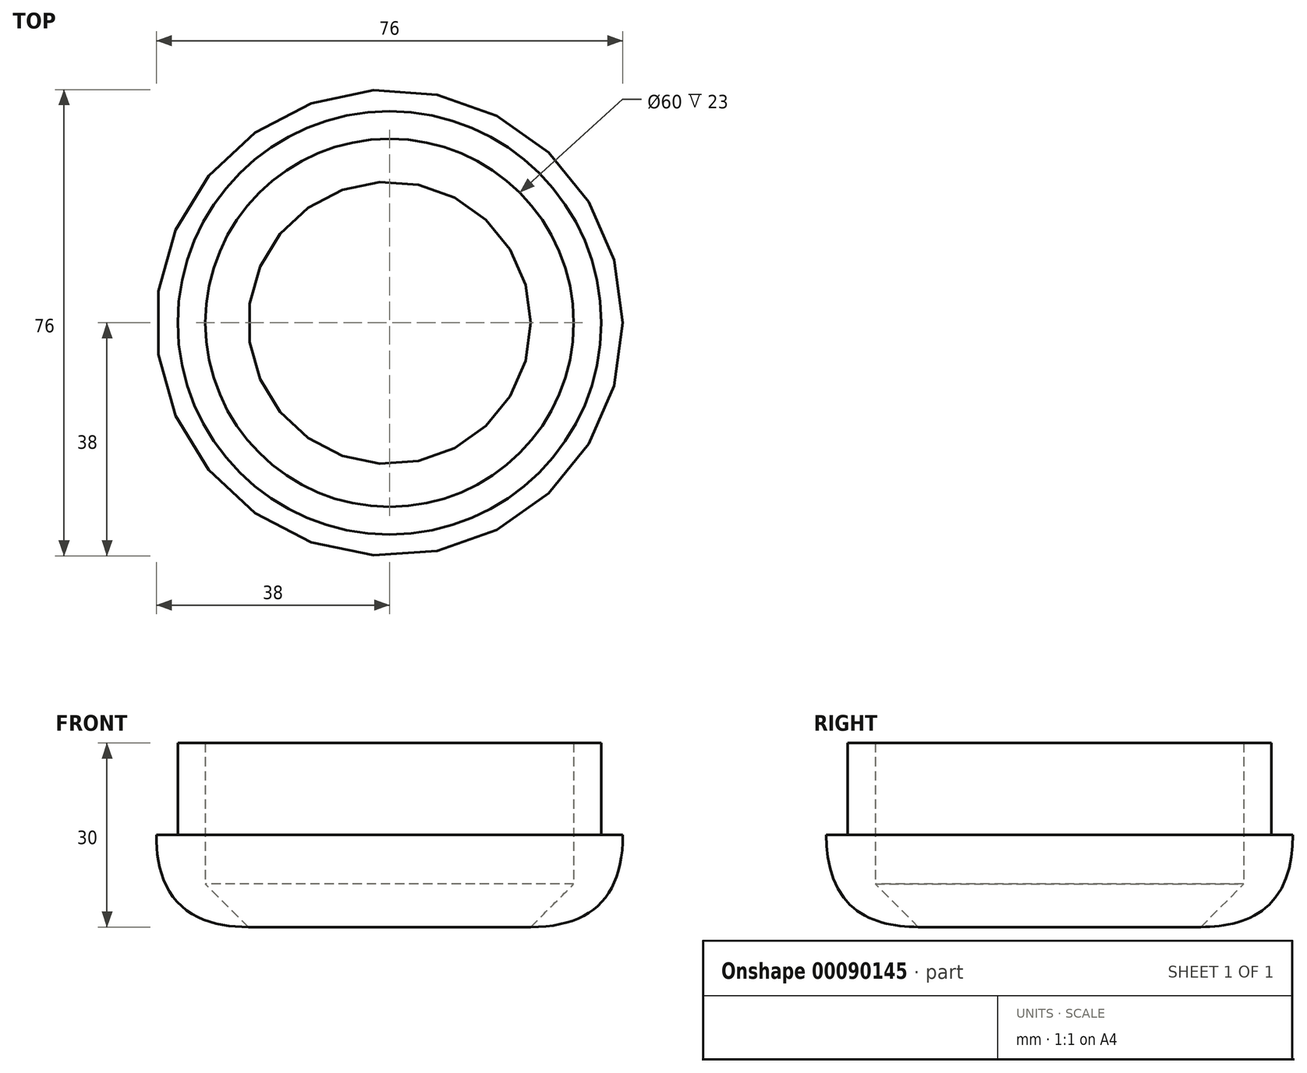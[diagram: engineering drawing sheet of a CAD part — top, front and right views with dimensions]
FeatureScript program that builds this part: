
annotation { "Feature Type Name" : "Feature", "Feature Type Description" : "" }
export const myFeature = defineFeature(function(context is Context, id is Id, definition is map)
    precondition{}
    {
        {
            var Q0;
            Q0=qCreatedBy(makeId("Top.planeOp"),FACE);
            var sketch = newSketch(context, id + "F0", { "sketchPlane" : qUnion([Q0])});
            skCircle(sketch, "E0", {"center": v(0, 0) * mm, "radius": 34.5 * mm});
            skCircle(sketch, "E1", {"center": v(0, 0) * mm, "radius": 30 * mm});
            skCircle(sketch, "E2", {"center": v(0, 0) * mm, "radius": 38 * mm});
            skCircle(sketch, "E3", {"center": v(0, 0) * mm, "radius": 23 * mm});
            skSolve(sketch);
        }
        {
            var Q0;
            Q0=qSketchRegion(id+"F0",true);
            extrude(context, id + "F1", {"entities" : qUnion([Q0]), "depth" : 15 * mm});
        }
        {
            var Q0;
            Q0=makeQuery(id+"F0.imprint","IMPRINT",FACE,{"disambiguationData":[TD([[makeQuery(id+"F0.imprint","IMPRINT",EDGE,{"derivedFrom":sQuery(id+"F0.wireOp",EDGE,"E0")}),1.0]])]});
            extrude(context, id + "F2", {"entities" : qUnion([Q0]), "operationType" : NewBodyOperationType.ADD, "depth" : 30 * mm});
        }
        {
            var Q0;
            Q0=qSketchRegion(id+"F0",true);
            var Q1;
            Q1=makeQuery(id+"F0.imprint","IMPRINT",FACE,{"disambiguationData":[TD([[makeQuery(id+"F0.imprint","IMPRINT",EDGE,{"derivedFrom":sQuery(id+"F0.wireOp",EDGE,"E1")}),1.0]])]});
            extrude(context, id + "F3", {"entities" : qUnion([Q0, Q1]), "operationType" : NewBodyOperationType.ADD, "depth" : 10 * mm});
        }
        {
            var Q0;
            Q0=makeQuery(id+"F3.opExtrude","CAP_EDGE",EDGE,{"disambiguationData":[OSD([sQuery(id+"F0.wireOp",EDGE,"E3")])],"isStart":false});
            chamfer(context, id + "F4", {"entities" : qUnion([Q0]), "width" : 10 * mm, "tangentPropagation" : true});
        }
        {
            var Q0;
            Q0=makeQuery(id+"F1.opExtrude","CAP_EDGE",EDGE,{"disambiguationData":[OSD([sQuery(id+"F0.wireOp",EDGE,"E2")])],"isStart":true});
            fillet(context, id + "F5", {"entities" : qUnion([Q0]), "radius" : 15 * mm, "tangentPropagation" : true, "rho" : 0.5, "crossSection" : FilletCrossSection.CONIC, "allowEdgeOverflow" : false});
        }
    });
